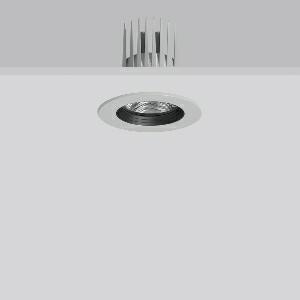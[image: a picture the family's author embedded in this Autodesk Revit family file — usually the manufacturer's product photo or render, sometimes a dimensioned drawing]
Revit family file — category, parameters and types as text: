
# Revit family: heledon_mini_e_901742_004_2_76_93c9
name_source: partatom
category: Lighting Fixtures
units: mm (PartAtom-declared; Revit-internal decimal feet)

## family parameters
Cut with Voids When Loaded = No
Host = Face
Light Source = No
Part Type = Normal
Room Calculation Point = No
Round Connector Dimension = Use Diameter
Shared = No

## types (1)
- HELEDON mini E (1 x LED Modul 927, 2400 lm, 2700)
    Apparent Load = 20 VA
    Approval mark = CE
    CIE Flux Codes = 95 99 100 100 100
    Color Rendering = 92
    Color Temperature = 2700
    Default Elevation = 1800 mm
    Description = Series: HELEDON mini
Round recessed downlight. Housing: die-cast aluminium, powder-coated. Black plastic ring and recessed LED to prevent glare from the side. Optical assembly with reflector made of MIRO-Silver with 98% total light reflection for outstanding efficiency - can be changed without tools. Best colour rendering index Ra>90. Suitable for Recessed ceiling mounting. Installation without tools thanks to spring fastening system. Including separate LED converter with connecting cable 600 mm.High quality converter without flickering and stroboscopic effect. Through-wiring box (5 pole) available as accessory. The following accessories can be mounted without use of tools: interchangeable lenses, decorative glasses, honeycomb louvre, clear and frosted diffusers, white interchangeable plastic ring. 
Colour: silver
Diameter: 124 mm
Height: 3 mm
Cut-out diameter: 114 mm
Recess height: 170 mm
Luminaire: recess height: 120 mm
Lamp: LED
Socket: without socket
Colour temperature: 2700K
Colour rendering index (CRI): 92
System power: 20 W
Rated luminous flux: 2400 lm
Luminous efficiency: 120 lm/W
Control gear: Converter, dimmable, DALI
Protection class: II
Type of protection: IP 20
    Height = 0 mm  [stored 0 ft]
    Lamp = 1 x LED Modul 927
    Lamp Light Flux = 2400 lm
    Lamp count = 1
    Length = 124 mm  [stored 0.406824 ft]
    Lifetime = 50000 h
    Luminous efficacy = 120 lm/W
    Manufacturer = RZB
    ModVariant = No
    Model = 901742.004.2.76
    Mounting Place = Ceiling
    Mounting Type = Recessed
    Number of Poles = 1
    OnlyDefault = Yes
    Power Factor = 1
    Product Name = HELEDON mini E
    Product group = Recessed downlights
    ProductGroupID = 402
    Protection Class = Protection class II
    Protection Degree = IP 20
    RLX_Detail_Level = 1
    RLX_Emergency_Light_Flux = 0 lm
    RLX_Emergency_Type = 0
    RLX_Emergency_Type_DB = No
    RlxData = <blob elided: 126933 chars, md5=54b9179f>
    Socket = socket
    Standby Power = 0 W
    System Light Flux = 2400 lm
    System Power = 20 W
    Type Comments = Product without accessories
    Type Image = 901657.004.jpg
    URL = http://relux.com
    VarID = ---
    Voltage = 230 V
    Voltage Range = 220-240 V
    Weight = 0.00 kg
    Width = 0 mm  [stored 0 ft]

note: [stored X ft] marks values corroborated as IEEE doubles in the binary element streams (Revit-internal decimal feet)

## geometry (parser evidence)
native form markers: Blend x4, Sweep x12
no freeform markers — native parametric forms only
